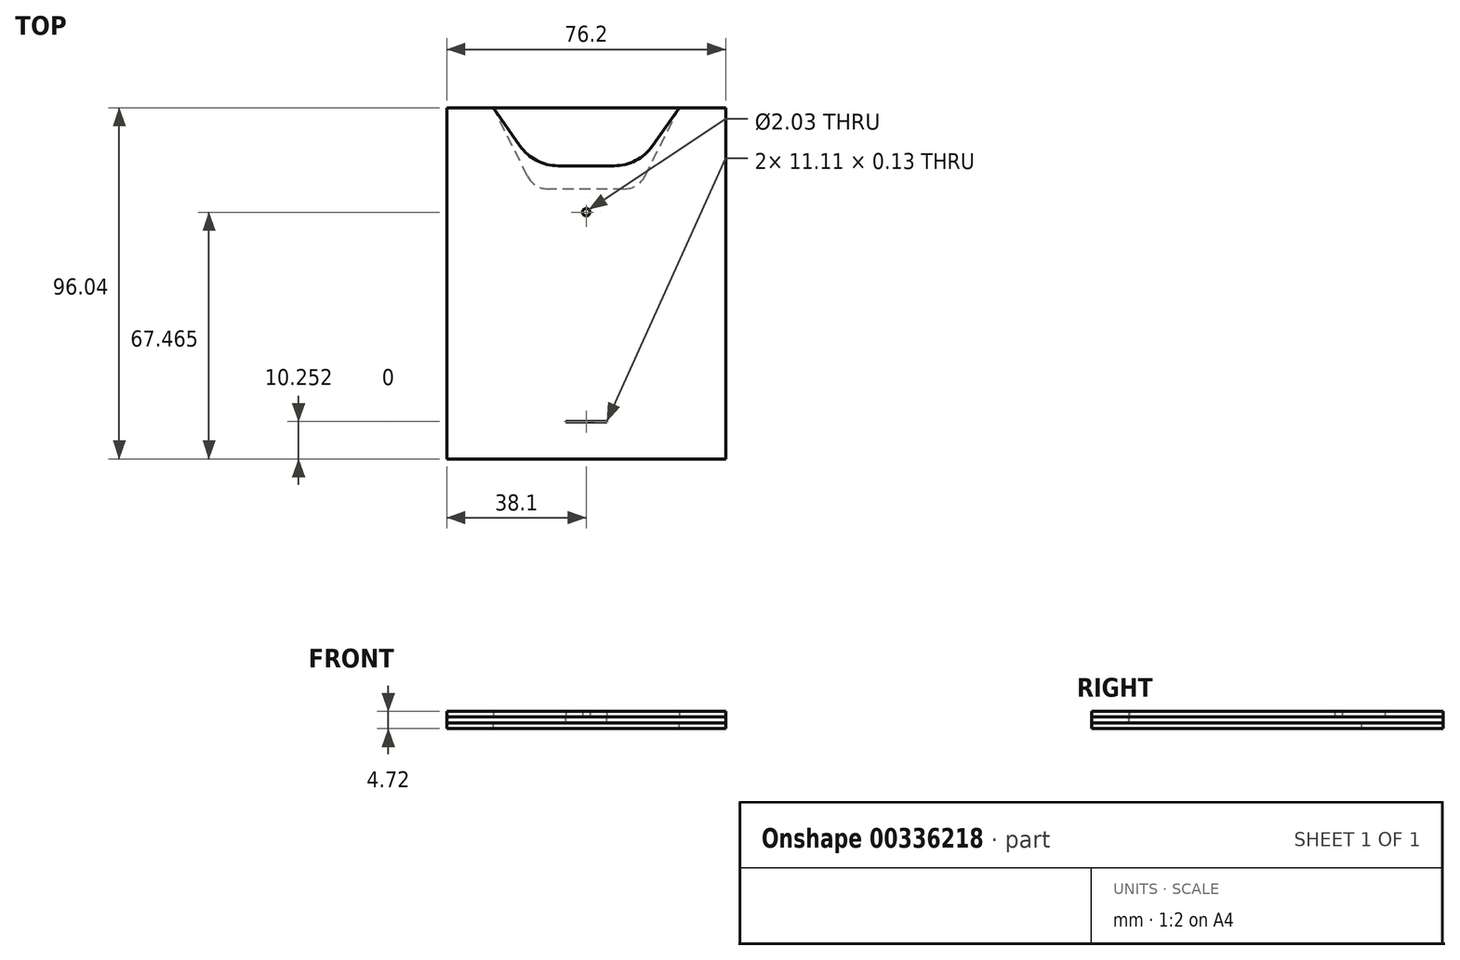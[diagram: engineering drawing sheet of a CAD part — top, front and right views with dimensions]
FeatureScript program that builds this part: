
annotation { "Feature Type Name" : "Feature", "Feature Type Description" : "" }
export const myFeature = defineFeature(function(context is Context, id is Id, definition is map)
    precondition{}
    {
        {
            var Q0;
            Q0=qCreatedBy(makeId("Top.planeOp"),FACE);
            var sketch = newSketch(context, id + "F0", { "sketchPlane" : qUnion([Q0])});
            skLineSegment(sketch, "E0.bottom", {"start": v(0, 0) * mm, "end": v(76.2, 0) * mm});
            skLineSegment(sketch, "E0.top", {"start": v(0, -96.04) * mm, "end": v(76.2, -96.04) * mm});
            skLineSegment(sketch, "E0.left", {"start": v(0, 0) * mm, "end": v(0, -96.04) * mm});
            skLineSegment(sketch, "E0.right", {"start": v(76.2, 0) * mm, "end": v(76.2, -96.04) * mm});
            skSolve(sketch);
        }
        {
            var Q0;
            Q0=makeQuery(id+"F0.imprint","IMPRINT",FACE,{"disambiguationData":[TD([[makeQuery(id+"F0.imprint","IMPRINT",EDGE,{"derivedFrom":sQuery(id+"F0.wireOp",EDGE,"E0.bottom")}),-1.0]])]});
            extrude(context, id + "F1", {"entities" : qUnion([Q0]), "depth" : 1.57 * mm});
        }
        {
            var Q0;
            Q0=makeQuery(id+"F1.opExtrude","CAP_FACE",FACE,{"disambiguationData":[OSD([sQuery(id+"F0.wireOp",EDGE,"E0.bottom"),sQuery(id+"F0.wireOp",EDGE,"E0.top"),sQuery(id+"F0.wireOp",EDGE,"E0.left"),sQuery(id+"F0.wireOp",EDGE,"E0.right")])],"isStart":false});
            var sketch = newSketch(context, id + "F2", { "sketchPlane" : qUnion([Q0])});
            skLineSegment(sketch, "E1.bottom", {"start": v(0, -96.04) * mm, "end": v(76.2, -96.04) * mm});
            skLineSegment(sketch, "E1.left", {"start": v(0, -96.04) * mm, "end": v(0, 0) * mm});
            skLineSegment(sketch, "E1.right", {"start": v(76.2, -96.04) * mm, "end": v(76.2, 0) * mm});
            skLineSegment(sketch, "E2.trimOffspring", {"start": v(63.5, 0) * mm, "end": v(76.2, 0) * mm});
            skLineSegment(sketch, "E3", {"start": v(38.1, -96.04) * mm, "end": v(38.1, -15.88) * mm, "construction": true});
            skPoint(sketch, "E4.orphan", {"position": v(23.81, -15.88) * mm});
            skLineSegment(sketch, "E5.MirrorCS", {"start": v(38.1, -15.88) * mm, "end": v(30.42, -15.88) * mm});
            skLineSegment(sketch, "E6.MirrorCS", {"start": v(20.02, -10.46) * mm, "end": v(12.7, 0) * mm});
            skLineSegment(sketch, "E7.MirrorCS", {"start": v(12.7, 0) * mm, "end": v(0, 0) * mm});
            skArc(sketch, "E8", {"start": v(20.02, -10.46) * mm, "mid": v(24.56, -14.44) * mm, "end": v(30.42, -15.88) * mm});
            skLineSegment(sketch, "E9", {"start": v(23.81, -15.88) * mm, "end": v(30.42, -15.88) * mm, "construction": true});
            skLineSegment(sketch, "E10", {"start": v(23.81, -15.88) * mm, "end": v(20.02, -10.46) * mm, "construction": true});
            skPoint(sketch, "E11.end.orphan", {"position": v(52.39, -15.88) * mm});
            skLineSegment(sketch, "E12.MirrorCS", {"start": v(56.18, -10.46) * mm, "end": v(63.5, 0) * mm});
            skArc(sketch, "E13.MirrorCS", {"start": v(56.18, -10.46) * mm, "mid": v(51.64, -14.44) * mm, "end": v(45.78, -15.88) * mm});
            skLineSegment(sketch, "E14.MirrorCS", {"start": v(38.1, -15.88) * mm, "end": v(45.78, -15.87) * mm});
            skCircle(sketch, "E15", {"center": v(38.1, -28.58) * mm, "radius": 1.02 * mm});
            skLineSegment(sketch, "E16", {"start": v(32.54, -85.73) * mm, "end": v(43.66, -85.73) * mm});
            skLineSegment(sketch, "E17", {"start": v(32.54, -85.73) * mm, "end": v(32.54, -85.85) * mm});
            skLineSegment(sketch, "E18", {"start": v(32.54, -85.85) * mm, "end": v(43.66, -85.85) * mm});
            skLineSegment(sketch, "E19", {"start": v(43.66, -85.85) * mm, "end": v(43.66, -85.73) * mm});
            skSolve(sketch);
        }
        {
            var Q0;
            Q0=makeQuery(id+"F2.imprint","IMPRINT",FACE,{"disambiguationData":[TD([[makeQuery(id+"F2.imprint","IMPRINT",EDGE,{"derivedFrom":sQuery(id+"F2.wireOp",EDGE,"E1.bottom")}),1.0]])]});
            extrude(context, id + "F3", {"entities" : qUnion([Q0]), "depth" : 1.57 * mm});
        }
        {
            var Q0;
            Q0=makeQuery(id+"F1.opExtrude","CAP_FACE",FACE,{"disambiguationData":[OSD([sQuery(id+"F0.wireOp",EDGE,"E0.bottom"),sQuery(id+"F0.wireOp",EDGE,"E0.top"),sQuery(id+"F0.wireOp",EDGE,"E0.left"),sQuery(id+"F0.wireOp",EDGE,"E0.right")])],"isStart":true});
            var sketch = newSketch(context, id + "F4", { "sketchPlane" : qUnion([Q0])});
            skLineSegment(sketch, "E20.bottom", {"start": v(0, 96.04) * mm, "end": v(76.2, 96.04) * mm});
            skLineSegment(sketch, "E20.top", {"start": v(0, 0) * mm, "end": v(12.7, 0) * mm});
            skLineSegment(sketch, "E20.left", {"start": v(0, 96.04) * mm, "end": v(0, 0) * mm});
            skLineSegment(sketch, "E20.right", {"start": v(76.2, 96.04) * mm, "end": v(76.2, 0) * mm});
            skLineSegment(sketch, "E21", {"start": v(38.1, 96.04) * mm, "end": v(38.1, 0) * mm, "construction": true});
            skLineSegment(sketch, "E22", {"start": v(38.1, 22.23) * mm, "end": v(27.74, 22.22) * mm});
            skLineSegment(sketch, "E23", {"start": v(22.06, 18.71) * mm, "end": v(12.7, 0) * mm});
            skLineSegment(sketch, "E24.trimOffspring", {"start": v(63.12, 0) * mm, "end": v(76.2, 0) * mm});
            skLineSegment(sketch, "E25.MirrorCS", {"start": v(54.14, 18.71) * mm, "end": v(63.5, 0) * mm});
            skLineSegment(sketch, "E26.MirrorCS", {"start": v(38.1, 22.23) * mm, "end": v(48.46, 22.22) * mm});
            skArc(sketch, "E27", {"start": v(54.14, 18.71) * mm, "mid": v(51.8, 21.28) * mm, "end": v(48.46, 22.23) * mm});
            skPoint(sketch, "E28.orphan", {"position": v(52.39, 22.22) * mm});
            skArc(sketch, "E29.MirrorCS", {"start": v(22.06, 18.71) * mm, "mid": v(24.4, 21.28) * mm, "end": v(27.74, 22.23) * mm});
            skPoint(sketch, "E30.orphan", {"position": v(23.81, 22.22) * mm});
            skSolve(sketch);
        }
        {
            var Q0;
            Q0=makeQuery(id+"F4.imprint","IMPRINT",FACE,{"disambiguationData":[TD([[makeQuery(id+"F4.imprint","IMPRINT",EDGE,{"derivedFrom":sQuery(id+"F4.wireOp",EDGE,"E20.bottom")}),-1.0]])]});
            extrude(context, id + "F5", {"entities" : qUnion([Q0]), "depth" : 1.57 * mm});
        }
        {
            var Q0;
            Q0=makeQuery(id+"F2.imprint","IMPRINT",FACE,{"disambiguationData":[TD([[makeQuery(id+"F2.imprint","IMPRINT",EDGE,{"derivedFrom":sQuery(id+"F2.wireOp",EDGE,"E16")}),-1.0]])]});
            extrude(context, id + "F6", {"entities" : qUnion([Q0]), "operationType" : NewBodyOperationType.REMOVE, "oppositeDirection" : true, "depth" : 1.57 * mm});
        }
    });
